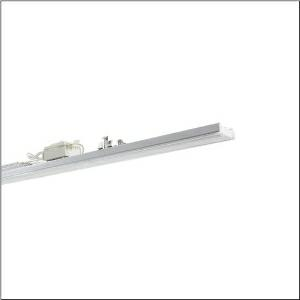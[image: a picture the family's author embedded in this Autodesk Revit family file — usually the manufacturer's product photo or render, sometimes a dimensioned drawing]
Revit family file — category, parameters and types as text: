
# Revit family: licross_r__21_recessed_ho_52tl12dv4lxm3s4_9b36
name_source: partatom
category: Lighting Fixtures
units: mm (PartAtom-declared; Revit-internal decimal feet)

## family parameters
Cut with Voids When Loaded = No
Host = Face
Light Source = No
Part Type = Normal
Room Calculation Point = No
Round Connector Dimension = Use Diameter
Shared = No

## types (1)
- --- (1 x LED, 20000 lm, 113.5 W, 4000K)
    Apparent Load = 114 VA
    CIE Flux Codes = 69 91 98 100 100
    Color Rendering = 80
    Color Temperature = 4000K
    Default Elevation = 1800 mm
    Description = Licross® 21 Recessed HO, luminaire insert, of sheet steel, galvanised, coil coated, white, length: 2.250mm, width: 66mm, height: 67mm, LED rated luminous flux: 20.000lm, light colour: 840, control gear: DALI 2, with plug, 6-pole, with phase selection, for trunking rail, 9 or 11-core, mains connection: 220..240V, AC, 50/60Hz, rated input power: 114W, for emergency light function, internal wiring halogen-free, for trunking rail, 9-/11-core, converter,control gear: single battery element, battery: LiFePO4, 9Ah, primary optical cover: cover, of PMMA, light emission: direct distribution, primary light characteristic: symmetric, protection rating (complete): IP40, insulation class (complete): insulation class I (protective earthing), certification: CE, UKCA, protection symbol: D if used in an environment without relevant dust loads with corresponding accessories, impact resistance: IK06, permissible ambient temperature for indoor applications: +5..+35°C, standard: EN 60598-2-22, corresponds to IFS (International Featured Standards) requirements for safety and quality in the food industry, reducing of maximum allowable ambient temperature of 5°C with ceiling mounting, LABS conformity tested according to VDMA 24364:2018-05, packaging unit: 1 piece
    Height = 58 mm
    Lamp = 1 x LED
    Lamp Light Flux = 20000 lm
    Lamp Power = 113.5 W
    Lamp count = 1
    Length = 2250 mm
    Luminous efficacy = 176 lm/W
    Manufacturer = Siteco
    ModVariant = No
    Model = 52TL12DV4LXM3S4
    Mounting Place = Ceiling
    Mounting Type = Pendant
    Number of Poles = 1
    OnlyDefault = Yes
    Power Factor = 1
    Product Name = Licross® 21 Recessed HO
    Product group = luminaire insert | ceiling pendant
    ProductGroupID = 902
    Protection Class = Protection class I
    Protection Degree = IP 40
    RLX_Detail_Level = 1
    RLX_Emergency_Light_Flux = 0 lm
    RLX_Emergency_Type = 0
    RLX_Emergency_Type_DB = No
    RlxData = <blob elided: 30085 chars, md5=a05a2c66>
    Socket = socket
    Standby Power = 0 W
    System Light Flux = 20000 lm
    System Power = 114 W
    Type Comments = : AC-mode, luminous flux: 100 % | dim-lin: 254 | 425 mA
    Type Image = l_1296930.jpg
    URL = http://relux.com
    VarID = @adj_041103
    Voltage = 0 V
    Weight = 0.00 kg
    Width = 66 mm

## geometry (parser evidence)
native form markers: Blend x4, Sweep x8
no freeform markers — native parametric forms only
